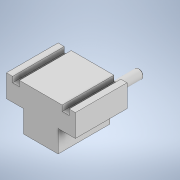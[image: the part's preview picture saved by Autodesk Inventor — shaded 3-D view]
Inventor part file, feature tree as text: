
AUTODESK INVENTOR PART (.ipt)
format: ipt  version: 2020 (Build 240168000, 168)  size: 152,064 bytes
history: native  units: in
note: dims shown in document units (in); Inventor stores cm internally (conversion verified against a paired STEP export)
features: extrude x4, sketch x4, chamfer x2, plane x1
ambient origin geometry x8: Origin, YZ Plane, XZ Plane, XY Plane, X Axis, Y Axis, Z Axis, Center Point
bodies: Solid1 (feature_tree)
feature tree (11):
  plane  "Work Plane1"
  extrude  "Extrusion1"  Depth=3.937in
  extrude  "Extrusion2"  Depth=2.5591in
  extrude  "Extrusion3"  Depth=5.9055in TaperAngle=0.0deg
  chamfer  "Chamfer1"  Distance=5.315in
  chamfer  "Chamfer2"  Distance=1.5748in
  extrude  "Extrusion4"  Depth=1.5748in
  sketch  "Sketch1"  dims[d0=7.874in d1=3.937in]
  sketch  "Sketch2"  dims[d2=7.4016in d3=2.5591in]
  sketch  "Sketch3"  dims[d5=1.9685in d6=5.9055in d7=0.0in]
  sketch  "Sketch4"  dims[d8=1.0236in d9=5.315in d10=0.0in d11=1.5748in d12=1.5748in d13=2.3622in d14=0.0in d15=0.1969in d16=0.0787in d17=45.0deg d18=0.0787in d19=0.0787in d20=45.0deg d21=2.5197in d22=0.7874in d23=0.6299in d24=0.7087in d25=0.0in d26=0.0in]
